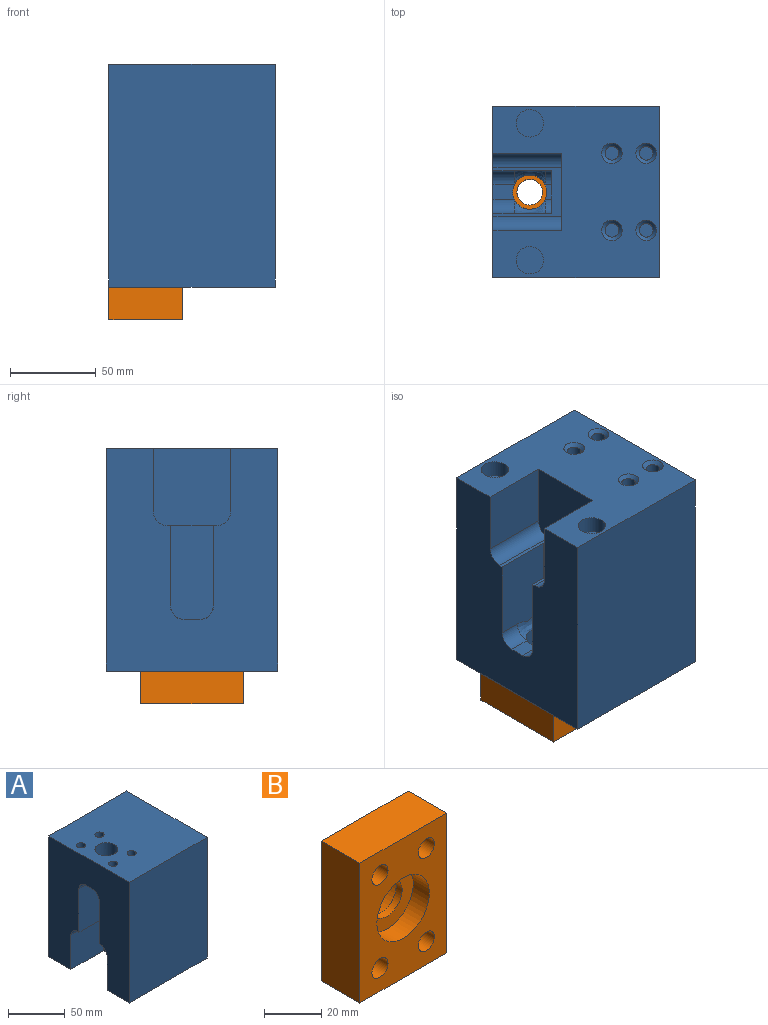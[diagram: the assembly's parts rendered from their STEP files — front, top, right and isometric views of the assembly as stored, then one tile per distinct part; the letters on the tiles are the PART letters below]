
ASSEMBLY  parts=2 mates=1
PART A: 60 faces, bbox 97x100x130 mm
  f0: plane 9x3.57mm, normal (0,0,-1), area 25.6mm2, adj f14,f15,f30,f33
  f1: plane 40x29mm, normal (0,0,-1), area 310mm2, adj f3,f10,f11,f12,f14,f34,f35
  f2: plane 100x97mm, normal (0,0,1), area 9184.8mm2, adj f3,f5,f6,f7,f15,f52,f54,f56
  f3: plane 130x100mm, normal (-1,0,0), area 9654.9mm2, adj f1,f2,f4,f6,f7,f8,f9,f11
  f4: plane 100x97mm, normal (0,0,-1), area 7045.5mm2, adj f3,f5,f6,f7,f8,f9,f10,f24
  f5: plane 130x100mm, normal (1,0,0), area 12384.2mm2, adj f2,f4,f6,f7,f48,f49,f50,f51
  f6: plane 130x97mm, normal (0,-1,0), area 12610mm2, adj f2,f3,f4,f5
  f7: plane 130x97mm, normal (0,1,0), area 12610mm2, adj f2,f3,f4,f5
  f8: plane 40x37mm, normal (0,-1,0), area 1480mm2, adj f3,f4,f10,f35
  f9: plane 40x37mm, normal (0,1,0), area 1480mm2, adj f3,f4,f10,f34
  f10: plane 45x45mm, normal (-1,0,0), area 1997.5mm2, adj f1,f4,f8,f9,f34,f35
  f11: plane 49.2x34mm, normal (0,-1,0), area 1615.7mm2, adj f1,f3,f14,f31,f32,f33
  f12: plane 49.19x34mm, normal (0,1,0), area 1615.7mm2, adj f1,f3,f14,f28,f29,f30
  f13: plane 12.57x9mm, normal (0,0,-1), area 106.6mm2, adj f3,f15,f28,f31
  f14: plane 55x25mm, normal (-1,0,0), area 1347.5mm2, adj f0,f1,f11,f12,f30,f33
  f15: cylinder r=10mm len=30mm, axis (0,0,1), area 1885mm2, adj f0,f2,f13,f29,f32
  f16: cylinder r=4mm len=28mm, axis (0,0,-1), area 703.7mm2, adj f17,f27
  f17: plane 8x8mm, normal (0,0,-1), area 50.3mm2, adj f16
  f18: cylinder r=4mm len=28mm, axis (0,0,-1), area 703.7mm2, adj f19,f26
  f19: plane 8x8mm, normal (0,0,-1), area 50.3mm2, adj f18
  f20: cylinder r=4mm len=28mm, axis (0,0,-1), area 703.7mm2, adj f21,f25
  f21: plane 8x8mm, normal (0,0,-1), area 50.3mm2, adj f20
  f22: cylinder r=4mm len=28mm, axis (0,0,-1), area 703.7mm2, adj f23,f24
  f23: plane 8x8mm, normal (0,0,-1), area 50.3mm2, adj f22
  f24: cone r=4mm half-angle=45deg, axis (0,0,-1), area 88.9mm2, adj f4,f22
  f25: cone r=4mm half-angle=45deg, axis (0,0,-1), area 88.9mm2, adj f4,f20
  f26: cone r=4mm half-angle=45deg, axis (0,0,-1), area 88.9mm2, adj f4,f18
  f27: cone r=4mm half-angle=45deg, axis (0,0,-1), area 88.9mm2, adj f4,f16
  f28: cylinder r=8mm len=12.57mm, axis (-1,0,0), area 158mm2, adj f3,f12,f13,f29
  f29: bspline ~20.71x8.56mm, area 154.9mm2, adj f12,f15,f28,f30
  f30: cylinder r=8mm len=8mm, axis (-1,0,0), area 44.9mm2, adj f0,f12,f14,f29
  f31: cylinder r=8mm len=12.57mm, axis (1,0,0), area 158mm2, adj f3,f11,f13,f32
  f32: bspline ~20.71x8.56mm, area 154.9mm2, adj f11,f15,f31,f33
  f33: cylinder r=8mm len=8mm, axis (1,0,0), area 44.9mm2, adj f0,f11,f14,f32
  f34: cylinder r=8mm len=40mm, axis (-1,0,0), area 502.7mm2, adj f1,f3,f9,f10
  f35: cylinder r=8mm len=40mm, axis (1,0,0), area 502.7mm2, adj f1,f3,f8,f10
  f36: cylinder r=8mm len=16mm, axis (0,0,-1), area 502.7mm2, adj f4,f37
  f37: plane 16x16mm, normal (0,0,-1), area 201.1mm2, adj f36
  f38: cylinder r=8mm len=16mm, axis (0,0,-1), area 502.7mm2, adj f4,f39
  f39: plane 16x16mm, normal (0,0,-1), area 201.1mm2, adj f38
  f40: cylinder r=5mm len=28mm, axis (1,0,0), area 879.6mm2, adj f41,f50
  f41: plane 10x10mm, normal (1,0,0), area 78.5mm2, adj f40
  f42: cylinder r=5mm len=28mm, axis (1,0,0), area 879.6mm2, adj f43,f48
  f43: plane 10x10mm, normal (1,0,0), area 78.5mm2, adj f42
  f44: cylinder r=5mm len=28mm, axis (1,0,0), area 879.6mm2, adj f45,f51
  f45: plane 10x10mm, normal (1,0,0), area 78.5mm2, adj f44
  f46: cylinder r=5mm len=28mm, axis (1,0,0), area 879.6mm2, adj f47,f49
  f47: plane 10x10mm, normal (1,0,0), area 78.5mm2, adj f46
  f48: cone r=5mm half-angle=45deg, axis (1,0,0), area 106.6mm2, adj f5,f42
  f49: cone r=5mm half-angle=45deg, axis (1,0,0), area 106.6mm2, adj f5,f46
  f50: cone r=5mm half-angle=45deg, axis (1,0,0), area 106.6mm2, adj f5,f40
  f51: cone r=5mm half-angle=45deg, axis (1,0,0), area 106.6mm2, adj f5,f44
  f52: cylinder r=4mm len=25mm, axis (0,0,1), area 628.3mm2, adj f2,f53
  f53: plane 8x8mm, normal (0,0,1), area 50.3mm2, adj f52
  f54: cylinder r=4mm len=25mm, axis (0,0,1), area 628.3mm2, adj f2,f55
  f55: plane 8x8mm, normal (0,0,1), area 50.3mm2, adj f54
  f56: cylinder r=4mm len=25mm, axis (0,0,1), area 628.3mm2, adj f2,f57
  f57: plane 8x8mm, normal (0,0,1), area 50.3mm2, adj f56
  f58: cylinder r=4mm len=25mm, axis (0,0,1), area 628.3mm2, adj f2,f59
  f59: plane 8x8mm, normal (0,0,1), area 50.3mm2, adj f58
PART B: 15 faces, bbox 43x19x60 mm
  f0: cylinder r=7.5mm len=15mm, axis (0,-1,0), area 141.4mm2, adj f7,f9
  f1: plane 43x19mm, normal (0,0,1), area 817mm2, adj f2,f4,f5,f6
  f2: plane 60x19mm, normal (-1,0,0), area 1140mm2, adj f1,f3,f5,f6
  f3: plane 43x19mm, normal (0,0,-1), area 817mm2, adj f2,f4,f5,f6
  f4: plane 60x19mm, normal (1,0,0), area 1140mm2, adj f1,f3,f5,f6
  f5: plane 60x43mm, normal (0,-1,0), area 1848mm2, adj f1,f2,f3,f4,f8,f11,f12,f13
  f6: plane 60x43mm, normal (0,1,0), area 1848mm2, adj f1,f2,f3,f4,f10,f11,f12,f13
  f7: plane 26x26mm, normal (0,-1,0), area 354.2mm2, adj f0,f8
  f8: cylinder r=13mm len=26mm, axis (0,-1,0), area 653.5mm2, adj f5,f7
  f9: plane 26x26mm, normal (0,1,0), area 354.2mm2, adj f0,f10
  f10: cylinder r=13mm len=26mm, axis (0,1,0), area 653.5mm2, adj f6,f9
  f11: cylinder r=4mm len=19mm, axis (0,-1,0), area 477.5mm2, adj f5,f6
  f12: cylinder r=4mm len=19mm, axis (0,-1,0), area 477.5mm2, adj f5,f6
  f13: cylinder r=4mm len=19mm, axis (0,-1,0), area 477.5mm2, adj f5,f6
  f14: cylinder r=4mm len=19mm, axis (0,-1,0), area 477.5mm2, adj f5,f6
PLACE A rot(axis=(1,0,0),180deg) t=(-126.06,-96.25,223.89)mm
PLACE B rot(axis=(-1,0,0),90deg) t=(-199.23,-73.49,114.13)mm
MATE fastened B.f11 <-> A.f52  axis (0,0,1) through (-259.1,-26.25,133.13)mm
